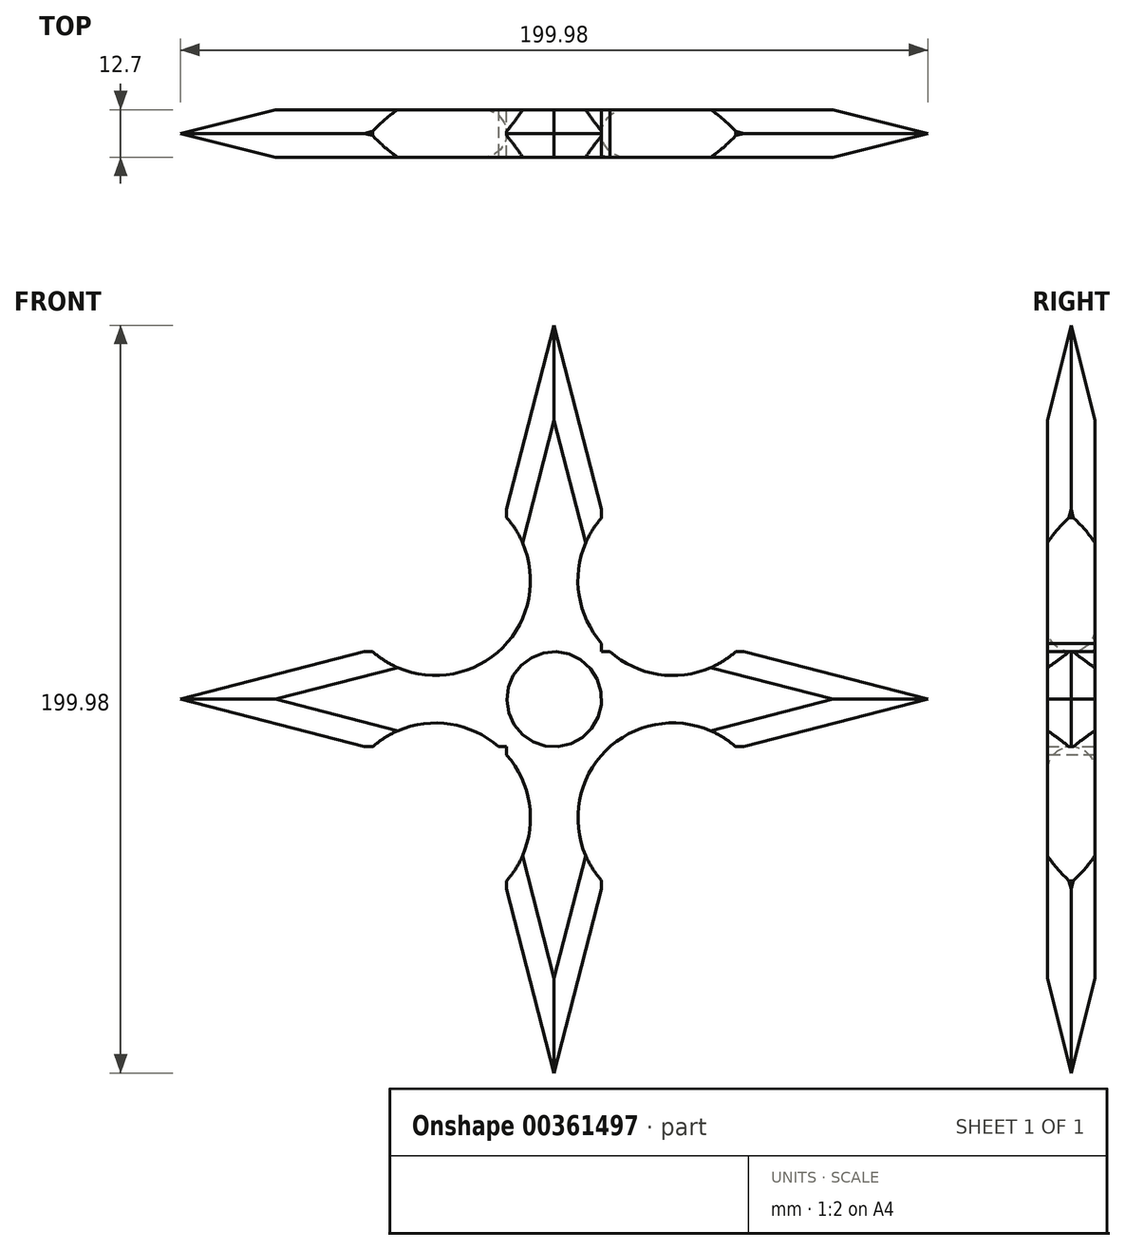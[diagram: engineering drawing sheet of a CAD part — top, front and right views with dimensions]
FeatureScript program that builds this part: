
annotation { "Feature Type Name" : "Feature", "Feature Type Description" : "" }
export const myFeature = defineFeature(function(context is Context, id is Id, definition is map)
    precondition{}
    {
        {
            var Q0;
            Q0=qCreatedBy(makeId("Front.planeOp"),FACE);
            var sketch = newSketch(context, id + "F0", { "sketchPlane" : qUnion([Q0])});
            skCircle(sketch, "E0", {"center": v(0, 0) * mm, "radius": 12.7 * mm});
            skCircle(sketch, "E1", {"center": v(0, 0) * mm, "radius": 19.05 * mm});
            skLineSegment(sketch, "E2.bottom", {"start": v(12.7, -50.8) * mm, "end": v(-12.7, -50.8) * mm});
            skLineSegment(sketch, "E2.top", {"start": v(12.7, 50.8) * mm, "end": v(-12.7, 50.8) * mm});
            skLineSegment(sketch, "E2.left", {"start": v(12.7, -50.8) * mm, "end": v(12.7, 50.8) * mm});
            skLineSegment(sketch, "E2.right", {"start": v(-12.7, -50.8) * mm, "end": v(-12.7, 50.8) * mm});
            skLineSegment(sketch, "E3.bottom", {"start": v(50.8, -12.7) * mm, "end": v(-50.8, -12.7) * mm});
            skLineSegment(sketch, "E3.top", {"start": v(50.8, 12.7) * mm, "end": v(-50.8, 12.7) * mm});
            skLineSegment(sketch, "E3.left", {"start": v(50.8, -12.7) * mm, "end": v(50.8, 12.7) * mm});
            skLineSegment(sketch, "E3.right", {"start": v(-50.8, -12.7) * mm, "end": v(-50.8, 12.7) * mm});
            skLineSegment(sketch, "E4.bottom", {"start": v(31.75, -31.75) * mm, "end": v(-31.75, -31.75) * mm});
            skLineSegment(sketch, "E4.top", {"start": v(31.75, 31.75) * mm, "end": v(-31.75, 31.75) * mm});
            skLineSegment(sketch, "E4.left", {"start": v(31.75, -31.75) * mm, "end": v(31.75, 31.75) * mm});
            skLineSegment(sketch, "E4.right", {"start": v(-31.75, -31.75) * mm, "end": v(-31.75, 31.75) * mm});
            skLineSegment(sketch, "E5", {"start": v(-50.8, -12.7) * mm, "end": v(-99.99, 0) * mm});
            skLineSegment(sketch, "E6", {"start": v(-99.99, 0) * mm, "end": v(-50.8, 12.7) * mm});
            skLineSegment(sketch, "E7", {"start": v(-12.7, -50.8) * mm, "end": v(0, -99.99) * mm});
            skLineSegment(sketch, "E8", {"start": v(0, -99.99) * mm, "end": v(12.7, -50.8) * mm});
            skLineSegment(sketch, "E9", {"start": v(50.8, -12.7) * mm, "end": v(99.99, 0) * mm});
            skLineSegment(sketch, "E10", {"start": v(99.99, 0) * mm, "end": v(50.8, 12.7) * mm});
            skLineSegment(sketch, "E11", {"start": v(12.7, 50.8) * mm, "end": v(0, 99.99) * mm});
            skPoint(sketch, "E11.endSnap0", {"position": v(0, 50.8) * mm});
            skLineSegment(sketch, "E12", {"start": v(0, 99.99) * mm, "end": v(-12.7, 50.8) * mm});
            skSolve(sketch);
        }
        {
            var Q0;
            {var subQ2=sQuery(id+"F0.wireOp",EDGE,"E2.left");var subQ4=sQuery(id+"F0.wireOp",EDGE,"E1");var subQ5=makeQuery(id+"F0.imprint","INTERSECT",VERTEX,{"disambiguationData":[OD(0.0)],"derivedFrom":[subQ4,subQ2]});Q0=makeQuery(id+"F0.imprint","IMPRINT",FACE,{"disambiguationData":[TD([[makeQuery(id+"F0.imprint","IMPRINT",EDGE,{"disambiguationData":[TD([[subQ5,-1.0]])],"derivedFrom":subQ4}),1.0]])]});}
            var Q1;
            {var subQ2=sQuery(id+"F0.wireOp",EDGE,"E3.top");var subQ5=sQuery(id+"F0.wireOp",EDGE,"E1");var subQ8=makeQuery(id+"F0.imprint","INTERSECT",VERTEX,{"disambiguationData":[OD(1.0)],"derivedFrom":[subQ5,subQ2]});Q1=makeQuery(id+"F0.imprint","IMPRINT",FACE,{"disambiguationData":[TD([[makeQuery(id+"F0.imprint","IMPRINT",EDGE,{"disambiguationData":[TD([[subQ8,-1.0]])],"derivedFrom":subQ5}),1.0]])]});}
            var Q2;
            {var subQ4=sQuery(id+"F0.wireOp",EDGE,"E1");var subQ6=sQuery(id+"F0.wireOp",EDGE,"E2.right");var subQ7=makeQuery(id+"F0.imprint","INTERSECT",VERTEX,{"disambiguationData":[OD(1.0)],"derivedFrom":[subQ4,subQ6]});Q2=makeQuery(id+"F0.imprint","IMPRINT",FACE,{"disambiguationData":[TD([[makeQuery(id+"F0.imprint","IMPRINT",EDGE,{"disambiguationData":[TD([[subQ7,-1.0]])],"derivedFrom":subQ4}),1.0]])]});}
            var Q3;
            {var subQ2=sQuery(id+"F0.wireOp",EDGE,"E3.top");var subQ4=sQuery(id+"F0.wireOp",EDGE,"E1");var subQ5=makeQuery(id+"F0.imprint","INTERSECT",VERTEX,{"disambiguationData":[OD(0.0)],"derivedFrom":[subQ4,subQ2]});Q3=makeQuery(id+"F0.imprint","IMPRINT",FACE,{"disambiguationData":[TD([[makeQuery(id+"F0.imprint","IMPRINT",EDGE,{"disambiguationData":[TD([[subQ5,1.0]])],"derivedFrom":subQ4}),1.0]])]});}
            var Q4;
            {var subQ0=sQuery(id+"F0.wireOp",EDGE,"E2.left");var subQ1=sQuery(id+"F0.wireOp",EDGE,"E0");var subQ2=makeQuery(id+"F0.imprint","INTERSECT",VERTEX,{"derivedFrom":[subQ1,subQ0]});Q4=makeQuery(id+"F0.imprint","IMPRINT",FACE,{"disambiguationData":[TD([[makeQuery(id+"F0.imprint","IMPRINT",EDGE,{"disambiguationData":[TD([[subQ2,1.0]])],"derivedFrom":subQ1}),-1.0]])]});}
            var Q5;
            {var subQ0=sQuery(id+"F0.wireOp",EDGE,"E2.right");var subQ1=sQuery(id+"F0.wireOp",EDGE,"E0");var subQ2=makeQuery(id+"F0.imprint","INTERSECT",VERTEX,{"derivedFrom":[subQ1,subQ0]});Q5=makeQuery(id+"F0.imprint","IMPRINT",FACE,{"disambiguationData":[TD([[makeQuery(id+"F0.imprint","IMPRINT",EDGE,{"disambiguationData":[TD([[subQ2,-1.0]])],"derivedFrom":subQ1}),-1.0]])]});}
            var Q6;
            {var subQ0=sQuery(id+"F0.wireOp",EDGE,"E3.top");var subQ1=sQuery(id+"F0.wireOp",EDGE,"E0");var subQ2=makeQuery(id+"F0.imprint","INTERSECT",VERTEX,{"derivedFrom":[subQ1,subQ0]});Q6=makeQuery(id+"F0.imprint","IMPRINT",FACE,{"disambiguationData":[TD([[makeQuery(id+"F0.imprint","IMPRINT",EDGE,{"disambiguationData":[TD([[subQ2,-1.0]])],"derivedFrom":subQ1}),-1.0]])]});}
            var Q7;
            {var subQ0=sQuery(id+"F0.wireOp",EDGE,"E3.top");var subQ1=sQuery(id+"F0.wireOp",EDGE,"E0");var subQ2=makeQuery(id+"F0.imprint","INTERSECT",VERTEX,{"derivedFrom":[subQ1,subQ0]});Q7=makeQuery(id+"F0.imprint","IMPRINT",FACE,{"disambiguationData":[TD([[makeQuery(id+"F0.imprint","IMPRINT",EDGE,{"disambiguationData":[TD([[subQ2,1.0]])],"derivedFrom":subQ1}),-1.0]])]});}
            var Q8;
            {var subQ3=sQuery(id+"F0.wireOp",EDGE,"E2.left");var subQ5=sQuery(id+"F0.wireOp",EDGE,"E1");var subQ6=makeQuery(id+"F0.imprint","INTERSECT",VERTEX,{"disambiguationData":[OD(0.0)],"derivedFrom":[subQ5,subQ3]});Q8=makeQuery(id+"F0.imprint","IMPRINT",FACE,{"disambiguationData":[TD([[makeQuery(id+"F0.imprint","IMPRINT",EDGE,{"disambiguationData":[TD([[subQ6,1.0]])],"derivedFrom":subQ5}),-1.0]])]});}
            var Q9;
            {var subQ0=sQuery(id+"F0.wireOp",EDGE,"E2.left");var subQ1=sQuery(id+"F0.wireOp",EDGE,"E1");var subQ2=makeQuery(id+"F0.imprint","INTERSECT",VERTEX,{"disambiguationData":[OD(0.0)],"derivedFrom":[subQ1,subQ0]});Q9=makeQuery(id+"F0.imprint","IMPRINT",FACE,{"disambiguationData":[TD([[makeQuery(id+"F0.imprint","IMPRINT",EDGE,{"disambiguationData":[TD([[subQ2,-1.0]])],"derivedFrom":subQ1}),-1.0]])]});}
            var Q10;
            {var subQ3=sQuery(id+"F0.wireOp",EDGE,"E1");var subQ7=sQuery(id+"F0.wireOp",EDGE,"E2.right");var subQ9=makeQuery(id+"F0.imprint","INTERSECT",VERTEX,{"disambiguationData":[OD(0.0)],"derivedFrom":[subQ3,subQ7]});Q10=makeQuery(id+"F0.imprint","IMPRINT",FACE,{"disambiguationData":[TD([[makeQuery(id+"F0.imprint","IMPRINT",EDGE,{"disambiguationData":[TD([[subQ9,-1.0]])],"derivedFrom":subQ3}),-1.0]])]});}
            var Q11;
            {var subQ0=sQuery(id+"F0.wireOp",EDGE,"E3.top");var subQ1=sQuery(id+"F0.wireOp",EDGE,"E1");var subQ2=makeQuery(id+"F0.imprint","INTERSECT",VERTEX,{"disambiguationData":[OD(1.0)],"derivedFrom":[subQ1,subQ0]});Q11=makeQuery(id+"F0.imprint","IMPRINT",FACE,{"disambiguationData":[TD([[makeQuery(id+"F0.imprint","IMPRINT",EDGE,{"disambiguationData":[TD([[subQ2,-1.0]])],"derivedFrom":subQ1}),-1.0]])]});}
            var Q12;
            {var subQ5=sQuery(id+"F0.wireOp",EDGE,"E3.bottom");var subQ7=sQuery(id+"F0.wireOp",EDGE,"E1");var subQ8=makeQuery(id+"F0.imprint","INTERSECT",VERTEX,{"disambiguationData":[OD(0.0)],"derivedFrom":[subQ7,subQ5]});Q12=makeQuery(id+"F0.imprint","IMPRINT",FACE,{"disambiguationData":[TD([[makeQuery(id+"F0.imprint","IMPRINT",EDGE,{"disambiguationData":[TD([[subQ8,-1.0]])],"derivedFrom":subQ7}),-1.0]])]});}
            var Q13;
            {var subQ0=sQuery(id+"F0.wireOp",EDGE,"E2.right");var subQ1=sQuery(id+"F0.wireOp",EDGE,"E1");var subQ2=makeQuery(id+"F0.imprint","INTERSECT",VERTEX,{"disambiguationData":[OD(1.0)],"derivedFrom":[subQ1,subQ0]});Q13=makeQuery(id+"F0.imprint","IMPRINT",FACE,{"disambiguationData":[TD([[makeQuery(id+"F0.imprint","IMPRINT",EDGE,{"disambiguationData":[TD([[subQ2,-1.0]])],"derivedFrom":subQ1}),-1.0]])]});}
            var Q14;
            {var subQ3=sQuery(id+"F0.wireOp",EDGE,"E2.left");var subQ5=sQuery(id+"F0.wireOp",EDGE,"E1");var subQ6=makeQuery(id+"F0.imprint","INTERSECT",VERTEX,{"disambiguationData":[OD(1.0)],"derivedFrom":[subQ5,subQ3]});Q14=makeQuery(id+"F0.imprint","IMPRINT",FACE,{"disambiguationData":[TD([[makeQuery(id+"F0.imprint","IMPRINT",EDGE,{"disambiguationData":[TD([[subQ6,-1.0]])],"derivedFrom":subQ5}),-1.0]])]});}
            var Q15;
            {var subQ0=sQuery(id+"F0.wireOp",EDGE,"E3.top");var subQ1=sQuery(id+"F0.wireOp",EDGE,"E1");var subQ2=makeQuery(id+"F0.imprint","INTERSECT",VERTEX,{"disambiguationData":[OD(0.0)],"derivedFrom":[subQ1,subQ0]});Q15=makeQuery(id+"F0.imprint","IMPRINT",FACE,{"disambiguationData":[TD([[makeQuery(id+"F0.imprint","IMPRINT",EDGE,{"disambiguationData":[TD([[subQ2,1.0]])],"derivedFrom":subQ1}),-1.0]])]});}
            var Q16;
            {var subQ0=sQuery(id+"F0.wireOp",EDGE,"E3.left");Q16=makeQuery(id+"F0.imprint","IMPRINT",FACE,{"disambiguationData":[TD([[makeQuery(id+"F0.imprint","IMPRINT",EDGE,{"derivedFrom":subQ0}),1.0]])]});}
            var Q17;
            Q17=makeQuery(id+"F0.imprint","IMPRINT",FACE,{"disambiguationData":[TD([[makeQuery(id+"F0.imprint","IMPRINT",EDGE,{"derivedFrom":sQuery(id+"F0.wireOp",EDGE,"E3.left")}),-1.0]])]});
            var Q18;
            Q18=makeQuery(id+"F0.imprint","IMPRINT",FACE,{"disambiguationData":[TD([[makeQuery(id+"F0.imprint","IMPRINT",EDGE,{"derivedFrom":sQuery(id+"F0.wireOp",EDGE,"E2.top")}),-1.0]])]});
            var Q19;
            {var subQ0=sQuery(id+"F0.wireOp",EDGE,"E2.top");Q19=makeQuery(id+"F0.imprint","IMPRINT",FACE,{"disambiguationData":[TD([[makeQuery(id+"F0.imprint","IMPRINT",EDGE,{"derivedFrom":subQ0}),1.0]])]});}
            var Q20;
            {var subQ0=sQuery(id+"F0.wireOp",EDGE,"E3.right");Q20=makeQuery(id+"F0.imprint","IMPRINT",FACE,{"disambiguationData":[TD([[makeQuery(id+"F0.imprint","IMPRINT",EDGE,{"derivedFrom":subQ0}),-1.0]])]});}
            var Q21;
            Q21=makeQuery(id+"F0.imprint","IMPRINT",FACE,{"disambiguationData":[TD([[makeQuery(id+"F0.imprint","IMPRINT",EDGE,{"derivedFrom":sQuery(id+"F0.wireOp",EDGE,"E3.right")}),1.0]])]});
            var Q22;
            Q22=makeQuery(id+"F0.imprint","IMPRINT",FACE,{"disambiguationData":[TD([[makeQuery(id+"F0.imprint","IMPRINT",EDGE,{"derivedFrom":sQuery(id+"F0.wireOp",EDGE,"E2.bottom")}),1.0]])]});
            var Q23;
            {var subQ0=sQuery(id+"F0.wireOp",EDGE,"E2.bottom");Q23=makeQuery(id+"F0.imprint","IMPRINT",FACE,{"disambiguationData":[TD([[makeQuery(id+"F0.imprint","IMPRINT",EDGE,{"derivedFrom":subQ0}),-1.0]])]});}
            var Q24;
            {var subQ0=sQuery(id+"F0.wireOp",EDGE,"E2.left");var subQ1=sQuery(id+"F0.wireOp",EDGE,"E1");var subQ2=makeQuery(id+"F0.imprint","INTERSECT",VERTEX,{"disambiguationData":[OD(1.0)],"derivedFrom":[subQ1,subQ0]});Q24=makeQuery(id+"F0.imprint","IMPRINT",FACE,{"disambiguationData":[TD([[makeQuery(id+"F0.imprint","IMPRINT",EDGE,{"disambiguationData":[TD([[subQ2,-1.0]])],"derivedFrom":subQ1}),1.0]])]});}
            var Q25;
            {var subQ0=sQuery(id+"F0.wireOp",EDGE,"E3.bottom");var subQ1=sQuery(id+"F0.wireOp",EDGE,"E1");var subQ2=makeQuery(id+"F0.imprint","INTERSECT",VERTEX,{"disambiguationData":[OD(0.0)],"derivedFrom":[subQ1,subQ0]});Q25=makeQuery(id+"F0.imprint","IMPRINT",FACE,{"disambiguationData":[TD([[makeQuery(id+"F0.imprint","IMPRINT",EDGE,{"disambiguationData":[TD([[subQ2,-1.0]])],"derivedFrom":subQ1}),1.0]])]});}
            var Q26;
            {var subQ0=sQuery(id+"F0.wireOp",EDGE,"E2.right");var subQ1=sQuery(id+"F0.wireOp",EDGE,"E1");var subQ2=makeQuery(id+"F0.imprint","INTERSECT",VERTEX,{"disambiguationData":[OD(0.0)],"derivedFrom":[subQ1,subQ0]});Q26=makeQuery(id+"F0.imprint","IMPRINT",FACE,{"disambiguationData":[TD([[makeQuery(id+"F0.imprint","IMPRINT",EDGE,{"disambiguationData":[TD([[subQ2,-1.0]])],"derivedFrom":subQ1}),1.0]])]});}
            var Q27;
            {var subQ0=sQuery(id+"F0.wireOp",EDGE,"E2.left");var subQ1=sQuery(id+"F0.wireOp",EDGE,"E1");var subQ2=makeQuery(id+"F0.imprint","INTERSECT",VERTEX,{"disambiguationData":[OD(0.0)],"derivedFrom":[subQ1,subQ0]});Q27=makeQuery(id+"F0.imprint","IMPRINT",FACE,{"disambiguationData":[TD([[makeQuery(id+"F0.imprint","IMPRINT",EDGE,{"disambiguationData":[TD([[subQ2,1.0]])],"derivedFrom":subQ1}),1.0]])]});}
            extrude(context, id + "F1", {"entities" : qUnion([Q0, Q1, Q2, Q3, Q4, Q5, Q6, Q7, Q8, Q9, Q10, Q11, Q12, Q13, Q14, Q15, Q16, Q17, Q18, Q19, Q20, Q21, Q22, Q23, Q24, Q25, Q26, Q27]), "depth" : 12.7 * mm});
        }
        {
            var Q0;
            Q0=makeQuery(id+"F1.opExtrude","CAP_FACE",FACE,{"disambiguationData":[OSD([sQuery(id+"F0.wireOp",EDGE,"E0"),sQuery(id+"F0.wireOp",EDGE,"E1"),sQuery(id+"F0.wireOp",EDGE,"E2.left"),sQuery(id+"F0.wireOp",EDGE,"E2.right"),sQuery(id+"F0.wireOp",EDGE,"E3.bottom"),sQuery(id+"F0.wireOp",EDGE,"E3.top"),sQuery(id+"F0.wireOp",EDGE,"E4.bottom"),sQuery(id+"F0.wireOp",EDGE,"E4.top"),sQuery(id+"F0.wireOp",EDGE,"E4.left"),sQuery(id+"F0.wireOp",EDGE,"E4.right"),sQuery(id+"F0.wireOp",EDGE,"E5"),sQuery(id+"F0.wireOp",EDGE,"E6"),sQuery(id+"F0.wireOp",EDGE,"E7"),sQuery(id+"F0.wireOp",EDGE,"E8"),sQuery(id+"F0.wireOp",EDGE,"E9"),sQuery(id+"F0.wireOp",EDGE,"E10"),sQuery(id+"F0.wireOp",EDGE,"E11"),sQuery(id+"F0.wireOp",EDGE,"E12")])],"isStart":false});
            var sketch = newSketch(context, id + "F2", { "sketchPlane" : qUnion([Q0])});
            skLineSegment(sketch, "E13", {"start": v(-31.75, 31.75) * mm, "end": v(31.75, 31.75) * mm});
            skLineSegment(sketch, "E14", {"start": v(31.75, 31.75) * mm, "end": v(31.75, -31.75) * mm});
            skLineSegment(sketch, "E15", {"start": v(31.75, -31.75) * mm, "end": v(-31.75, -31.75) * mm});
            skLineSegment(sketch, "E16", {"start": v(-31.75, -31.75) * mm, "end": v(-31.75, 31.75) * mm});
            skSolve(sketch);
        }
        {
            var Q0;
            Q0=sQuery(id+"F2.wireOp",VERTEX,"E13.start");
            var Q1;
            Q1=sQuery(id+"F2.wireOp",VERTEX,"E16.start");
            var Q2;
            Q2=sQuery(id+"F2.wireOp",VERTEX,"E15.start");
            var Q3;
            Q3=sQuery(id+"F2.wireOp",VERTEX,"E14.start");
            var Q4;
            Q4=makeQuery(id+"F1.opExtrude","SWEPT_BODY",BODY,{"disambiguationData":[OSD([sQuery(id+"F0.wireOp",EDGE,"E0"),sQuery(id+"F0.wireOp",EDGE,"E1"),sQuery(id+"F0.wireOp",EDGE,"E2.left"),sQuery(id+"F0.wireOp",EDGE,"E2.right"),sQuery(id+"F0.wireOp",EDGE,"E3.bottom"),sQuery(id+"F0.wireOp",EDGE,"E3.top"),sQuery(id+"F0.wireOp",EDGE,"E4.bottom"),sQuery(id+"F0.wireOp",EDGE,"E4.top"),sQuery(id+"F0.wireOp",EDGE,"E4.left"),sQuery(id+"F0.wireOp",EDGE,"E4.right"),sQuery(id+"F0.wireOp",EDGE,"E5"),sQuery(id+"F0.wireOp",EDGE,"E6"),sQuery(id+"F0.wireOp",EDGE,"E7"),sQuery(id+"F0.wireOp",EDGE,"E8"),sQuery(id+"F0.wireOp",EDGE,"E9"),sQuery(id+"F0.wireOp",EDGE,"E10"),sQuery(id+"F0.wireOp",EDGE,"E11"),sQuery(id+"F0.wireOp",EDGE,"E12")])]});
            hole(context, id + "F3", {"style" : HoleStyle.SIMPLE, "endStyle" : HoleEndStyle.THROUGH, "holeDiameter" : 50.8 * mm, "tappedDepth" : 12.7 * mm, "tapClearance" : 3, "locations" : qUnion([Q0, Q1, Q2, Q3]), "scope" : qUnion([Q4])});
        }
        {
            var Q0;
            Q0=makeQuery(id+"F1.opExtrude","CAP_EDGE",EDGE,{"disambiguationData":[OSD([sQuery(id+"F0.wireOp",EDGE,"E6")])],"isStart":false});
            var Q1;
            Q1=makeQuery(id+"F1.opExtrude","CAP_EDGE",EDGE,{"disambiguationData":[OSD([sQuery(id+"F0.wireOp",EDGE,"E5")])],"isStart":false});
            var Q2;
            Q2=makeQuery(id+"F1.opExtrude","CAP_EDGE",EDGE,{"disambiguationData":[OSD([sQuery(id+"F0.wireOp",EDGE,"E5")])],"isStart":true});
            var Q3;
            Q3=makeQuery(id+"F1.opExtrude","CAP_EDGE",EDGE,{"disambiguationData":[OSD([sQuery(id+"F0.wireOp",EDGE,"E6")])],"isStart":true});
            var Q4;
            Q4=makeQuery(id+"F1.opExtrude","CAP_EDGE",EDGE,{"disambiguationData":[OSD([sQuery(id+"F0.wireOp",EDGE,"E11")])],"isStart":false});
            var Q5;
            Q5=makeQuery(id+"F1.opExtrude","CAP_EDGE",EDGE,{"disambiguationData":[OSD([sQuery(id+"F0.wireOp",EDGE,"E12")])],"isStart":false});
            var Q6;
            Q6=makeQuery(id+"F1.opExtrude","CAP_EDGE",EDGE,{"disambiguationData":[OSD([sQuery(id+"F0.wireOp",EDGE,"E12")])],"isStart":true});
            var Q7;
            Q7=makeQuery(id+"F1.opExtrude","CAP_EDGE",EDGE,{"disambiguationData":[OSD([sQuery(id+"F0.wireOp",EDGE,"E11")])],"isStart":true});
            var Q8;
            Q8=makeQuery(id+"F1.opExtrude","CAP_EDGE",EDGE,{"disambiguationData":[OSD([sQuery(id+"F0.wireOp",EDGE,"E10")])],"isStart":true});
            var Q9;
            Q9=makeQuery(id+"F1.opExtrude","CAP_EDGE",EDGE,{"disambiguationData":[OSD([sQuery(id+"F0.wireOp",EDGE,"E10")])],"isStart":false});
            var Q10;
            Q10=makeQuery(id+"F1.opExtrude","CAP_EDGE",EDGE,{"disambiguationData":[OSD([sQuery(id+"F0.wireOp",EDGE,"E9")])],"isStart":true});
            var Q11;
            Q11=makeQuery(id+"F1.opExtrude","CAP_EDGE",EDGE,{"disambiguationData":[OSD([sQuery(id+"F0.wireOp",EDGE,"E9")])],"isStart":false});
            var Q12;
            Q12=makeQuery(id+"F1.opExtrude","CAP_EDGE",EDGE,{"disambiguationData":[OSD([sQuery(id+"F0.wireOp",EDGE,"E7")])],"isStart":true});
            var Q13;
            Q13=makeQuery(id+"F1.opExtrude","CAP_EDGE",EDGE,{"disambiguationData":[OSD([sQuery(id+"F0.wireOp",EDGE,"E8")])],"isStart":true});
            var Q14;
            Q14=makeQuery(id+"F1.opExtrude","CAP_EDGE",EDGE,{"disambiguationData":[OSD([sQuery(id+"F0.wireOp",EDGE,"E8")])],"isStart":false});
            var Q15;
            Q15=makeQuery(id+"F1.opExtrude","CAP_EDGE",EDGE,{"disambiguationData":[OSD([sQuery(id+"F0.wireOp",EDGE,"E7")])],"isStart":false});
            chamfer(context, id + "F4", {"entities" : qUnion([Q0, Q1, Q2, Q3, Q4, Q5, Q6, Q7, Q8, Q9, Q10, Q11, Q12, Q13, Q14, Q15]), "chamferType" : ChamferType.OFFSET_ANGLE, "width" : 6.35 * mm, "oppositeDirection" : false, "angle" : 45 * degree, "tangentPropagation" : true});
        }
        {
            var Q0;
            Q0=makeQuery(id+"F1.opExtrude","CAP_EDGE",EDGE,{"disambiguationData":[OSD([sQuery(id+"F0.wireOp",EDGE,"E0")])],"isStart":true});
            var Q1;
            Q1=makeQuery(id+"F1.opExtrude","CAP_EDGE",EDGE,{"disambiguationData":[OSD([sQuery(id+"F0.wireOp",EDGE,"E0")])],"isStart":false});
            var Q2;
            Q2=makeQuery(id+"F3.hole-2.boolean.opBoolean","INTERSECT",EDGE,{"derivedFrom":[makeQuery(id+"F1.opExtrude","CAP_FACE",FACE,{"disambiguationData":[OSD([sQuery(id+"F0.wireOp",EDGE,"E0"),sQuery(id+"F0.wireOp",EDGE,"E2.left"),sQuery(id+"F0.wireOp",EDGE,"E2.right"),sQuery(id+"F0.wireOp",EDGE,"E3.bottom"),sQuery(id+"F0.wireOp",EDGE,"E3.top"),sQuery(id+"F0.wireOp",EDGE,"E4.bottom"),sQuery(id+"F0.wireOp",EDGE,"E4.top"),sQuery(id+"F0.wireOp",EDGE,"E4.left"),sQuery(id+"F0.wireOp",EDGE,"E4.right"),sQuery(id+"F0.wireOp",EDGE,"E5"),sQuery(id+"F0.wireOp",EDGE,"E6"),sQuery(id+"F0.wireOp",EDGE,"E7"),sQuery(id+"F0.wireOp",EDGE,"E8"),sQuery(id+"F0.wireOp",EDGE,"E9"),sQuery(id+"F0.wireOp",EDGE,"E10"),sQuery(id+"F0.wireOp",EDGE,"E11"),sQuery(id+"F0.wireOp",EDGE,"E12")])],"isStart":true}),makeQuery(id+"F3.hole-2.opRevolve","SWEPT_FACE",FACE,{"disambiguationData":[OSD([sQuery(id+"F3.hole-2.sketch.wireOp",EDGE,"core_line_2")])]})]});
            var Q3;
            Q3=makeQuery(id+"F3.hole-1.boolean.opBoolean","INTERSECT",EDGE,{"derivedFrom":[makeQuery(id+"F1.opExtrude","CAP_FACE",FACE,{"disambiguationData":[OSD([sQuery(id+"F0.wireOp",EDGE,"E0"),sQuery(id+"F0.wireOp",EDGE,"E2.left"),sQuery(id+"F0.wireOp",EDGE,"E2.right"),sQuery(id+"F0.wireOp",EDGE,"E3.bottom"),sQuery(id+"F0.wireOp",EDGE,"E3.top"),sQuery(id+"F0.wireOp",EDGE,"E4.bottom"),sQuery(id+"F0.wireOp",EDGE,"E4.top"),sQuery(id+"F0.wireOp",EDGE,"E4.left"),sQuery(id+"F0.wireOp",EDGE,"E4.right"),sQuery(id+"F0.wireOp",EDGE,"E5"),sQuery(id+"F0.wireOp",EDGE,"E6"),sQuery(id+"F0.wireOp",EDGE,"E7"),sQuery(id+"F0.wireOp",EDGE,"E8"),sQuery(id+"F0.wireOp",EDGE,"E9"),sQuery(id+"F0.wireOp",EDGE,"E10"),sQuery(id+"F0.wireOp",EDGE,"E11"),sQuery(id+"F0.wireOp",EDGE,"E12")])],"isStart":true}),makeQuery(id+"F3.hole-1.opRevolve","SWEPT_FACE",FACE,{"disambiguationData":[OSD([sQuery(id+"F3.hole-1.sketch.wireOp",EDGE,"core_line_2")])]})]});
            var Q4;
            Q4=makeQuery(id+"F3.hole-3.boolean.opBoolean","INTERSECT",EDGE,{"derivedFrom":[makeQuery(id+"F1.opExtrude","CAP_FACE",FACE,{"disambiguationData":[OSD([sQuery(id+"F0.wireOp",EDGE,"E0"),sQuery(id+"F0.wireOp",EDGE,"E2.left"),sQuery(id+"F0.wireOp",EDGE,"E2.right"),sQuery(id+"F0.wireOp",EDGE,"E3.bottom"),sQuery(id+"F0.wireOp",EDGE,"E3.top"),sQuery(id+"F0.wireOp",EDGE,"E4.bottom"),sQuery(id+"F0.wireOp",EDGE,"E4.top"),sQuery(id+"F0.wireOp",EDGE,"E4.left"),sQuery(id+"F0.wireOp",EDGE,"E4.right"),sQuery(id+"F0.wireOp",EDGE,"E5"),sQuery(id+"F0.wireOp",EDGE,"E6"),sQuery(id+"F0.wireOp",EDGE,"E7"),sQuery(id+"F0.wireOp",EDGE,"E8"),sQuery(id+"F0.wireOp",EDGE,"E9"),sQuery(id+"F0.wireOp",EDGE,"E10"),sQuery(id+"F0.wireOp",EDGE,"E11"),sQuery(id+"F0.wireOp",EDGE,"E12")])],"isStart":true}),makeQuery(id+"F3.hole-3.opRevolve","SWEPT_FACE",FACE,{"disambiguationData":[OSD([sQuery(id+"F3.hole-3.sketch.wireOp",EDGE,"core_line_2")])]})]});
            var Q5;
            Q5=makeQuery(id+"F3.hole-3.boolean.opBoolean","COPY",EDGE,{"derivedFrom":makeQuery(id+"F3.hole-3.opRevolve","SWEPT_EDGE",EDGE,{"disambiguationData":[OSD([sQuery(id+"F3.hole-3.sketch.wireOp",EDGE,"core_line_2"),sQuery(id+"F3.hole-3.sketch.wireOp",EDGE,"core_line_3")])]})});
            var Q6;
            Q6=makeQuery(id+"F3.hole-0.boolean.opBoolean","INTERSECT",EDGE,{"derivedFrom":[makeQuery(id+"F1.opExtrude","CAP_FACE",FACE,{"disambiguationData":[OSD([sQuery(id+"F0.wireOp",EDGE,"E0"),sQuery(id+"F0.wireOp",EDGE,"E2.left"),sQuery(id+"F0.wireOp",EDGE,"E2.right"),sQuery(id+"F0.wireOp",EDGE,"E3.bottom"),sQuery(id+"F0.wireOp",EDGE,"E3.top"),sQuery(id+"F0.wireOp",EDGE,"E4.bottom"),sQuery(id+"F0.wireOp",EDGE,"E4.top"),sQuery(id+"F0.wireOp",EDGE,"E4.left"),sQuery(id+"F0.wireOp",EDGE,"E4.right"),sQuery(id+"F0.wireOp",EDGE,"E5"),sQuery(id+"F0.wireOp",EDGE,"E6"),sQuery(id+"F0.wireOp",EDGE,"E7"),sQuery(id+"F0.wireOp",EDGE,"E8"),sQuery(id+"F0.wireOp",EDGE,"E9"),sQuery(id+"F0.wireOp",EDGE,"E10"),sQuery(id+"F0.wireOp",EDGE,"E11"),sQuery(id+"F0.wireOp",EDGE,"E12")])],"isStart":true}),makeQuery(id+"F3.hole-0.opRevolve","SWEPT_FACE",FACE,{"disambiguationData":[OSD([sQuery(id+"F3.hole-0.sketch.wireOp",EDGE,"core_line_2")])]})]});
            var Q7;
            Q7=makeQuery(id+"F3.hole-0.boolean.opBoolean","COPY",EDGE,{"derivedFrom":makeQuery(id+"F3.hole-0.opRevolve","SWEPT_EDGE",EDGE,{"disambiguationData":[OSD([sQuery(id+"F3.hole-0.sketch.wireOp",EDGE,"core_line_2"),sQuery(id+"F3.hole-0.sketch.wireOp",EDGE,"core_line_3")])]})});
            var Q8;
            Q8=makeQuery(id+"F3.hole-2.boolean.opBoolean","COPY",EDGE,{"derivedFrom":makeQuery(id+"F3.hole-2.opRevolve","SWEPT_EDGE",EDGE,{"disambiguationData":[OSD([sQuery(id+"F3.hole-2.sketch.wireOp",EDGE,"core_line_2"),sQuery(id+"F3.hole-2.sketch.wireOp",EDGE,"core_line_3")])]})});
            fillet(context, id + "F5", {"entities" : qUnion([Q0, Q1, Q2, Q3, Q4, Q5, Q6, Q7, Q8]), "radius" : 6.35 * mm, "tangentPropagation" : true, "allowEdgeOverflow" : false});
        }
    });
